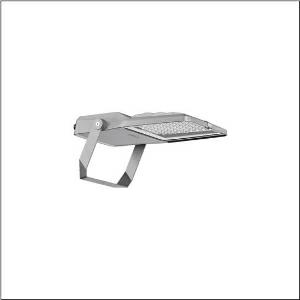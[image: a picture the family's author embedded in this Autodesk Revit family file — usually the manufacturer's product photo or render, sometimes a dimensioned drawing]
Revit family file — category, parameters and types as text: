
# Revit family: floodlight_fl_21_mini___pl33t_5xa7775c2f1a_de84
name_source: partatom
category: Lighting Fixtures
units: mm (PartAtom-declared; Revit-internal decimal feet)

## family parameters
Cut with Voids When Loaded = No
Host = Face
Light Source = No
Part Type = Normal
Room Calculation Point = No
Round Connector Dimension = Use Diameter
Shared = No

## types (1)
- --- (1 x LED, 12050 lm, 89 W, 3000K)
    Apparent Load = 89 VA
    CIE Flux Codes = 26 75 99 100 100
    Color Rendering = 70
    Color Temperature = 3000K
    Default Elevation = 1800 mm
    Description = Floodlight FL 21 mini, floodlight, primary light control with lens, of PMMA, primary optical cover: protective disc, of toughened safety glass, transparent, light distribution: PL33T, light emission: direct distribution, installation type: surface-mounted, LED, High Power LED, rated luminous flux: 12.050lm, luminous efficacy: 135lm/W, light colour: 730, colour temperature: 3000K, control gear: Smart Interface (Zhaga), control: flexible luminous flux parameterisation, time-dependent luminous flux control, constant luminous flux control, overheat protection, pre-setting: logarithmic dimming characteristic, with terminal, 6-pole, mains connection: 220..240V, AC, 50/60Hz, start of lifetime: 89W, end of service life: 94W, reduction: 43W, luminaire housing, of diecast aluminium, powder-coated, Siteco® metallic grey (DB 702S), corrosivity category C5 mid according to DIN EN ISO 12944, suitable for swimming pools, chlorine-resistant, sealing non-destructively replaceable, mounting bracket, of steel, galvanised, powder-coated, Siteco® metallic grey (DB 702S), Smart Interface above, protection rating (complete): IP66, insulation class (complete): insulation class II (safety insulation), certification: CE, ENEC, VDE, protection symbol: D, impact resistance: IK08, permissible operating ambient temperature: -40..+40°C, permissible operating ambient temperature for outdoor applications: -40..+50°C, standard: DIN EN 12944, LABS conformity tested according to VDMA 24364:2018-05, packaging unit: 1 piece

Light Distribution: PL33T
    Height = 70 mm
    Lamp = 1 x LED
    Lamp Light Flux = 12050 lm
    Lamp Power = 89 W
    Lamp count = 1
    Length = 485 mm
    Luminous efficacy = 135 lm/W
    Manufacturer = Siteco
    ModVariant = No
    Model = 5XA7775C2F1A
    Number of Poles = 1
    OnlyDefault = Yes
    Power Factor = 1
    Product Name = Floodlight FL 21 mini | PL33T
    Product group = floodlight | pylon annexe
    ProductGroupID = 6200
    Protection Class = Protection class II
    Protection Degree = IP 66
    RLX_Detail_Level = 1
    RLX_Emergency_Light_Flux = 0 lm
    RLX_Emergency_Type = 0
    RLX_Emergency_Type_DB = No
    RlxData = <blob elided: 95833 chars, md5=ee7b483b>
    Socket = socket
    Standby Power = 0 W
    System Light Flux = 12050 lm
    System Power = 89 W
    Type Comments = factory setting: luminous flux: 100 % | dim-lin: 254 | 456 mA
    Type Image = l_1006845.jpg
    URL = http://relux.com
    VarID = @adj_148574
    Voltage = 0 V
    Weight = 0.00 kg
    Width = 337 mm

## geometry (parser evidence)
native form markers: Blend x4, Sweep x13
no freeform markers — native parametric forms only
